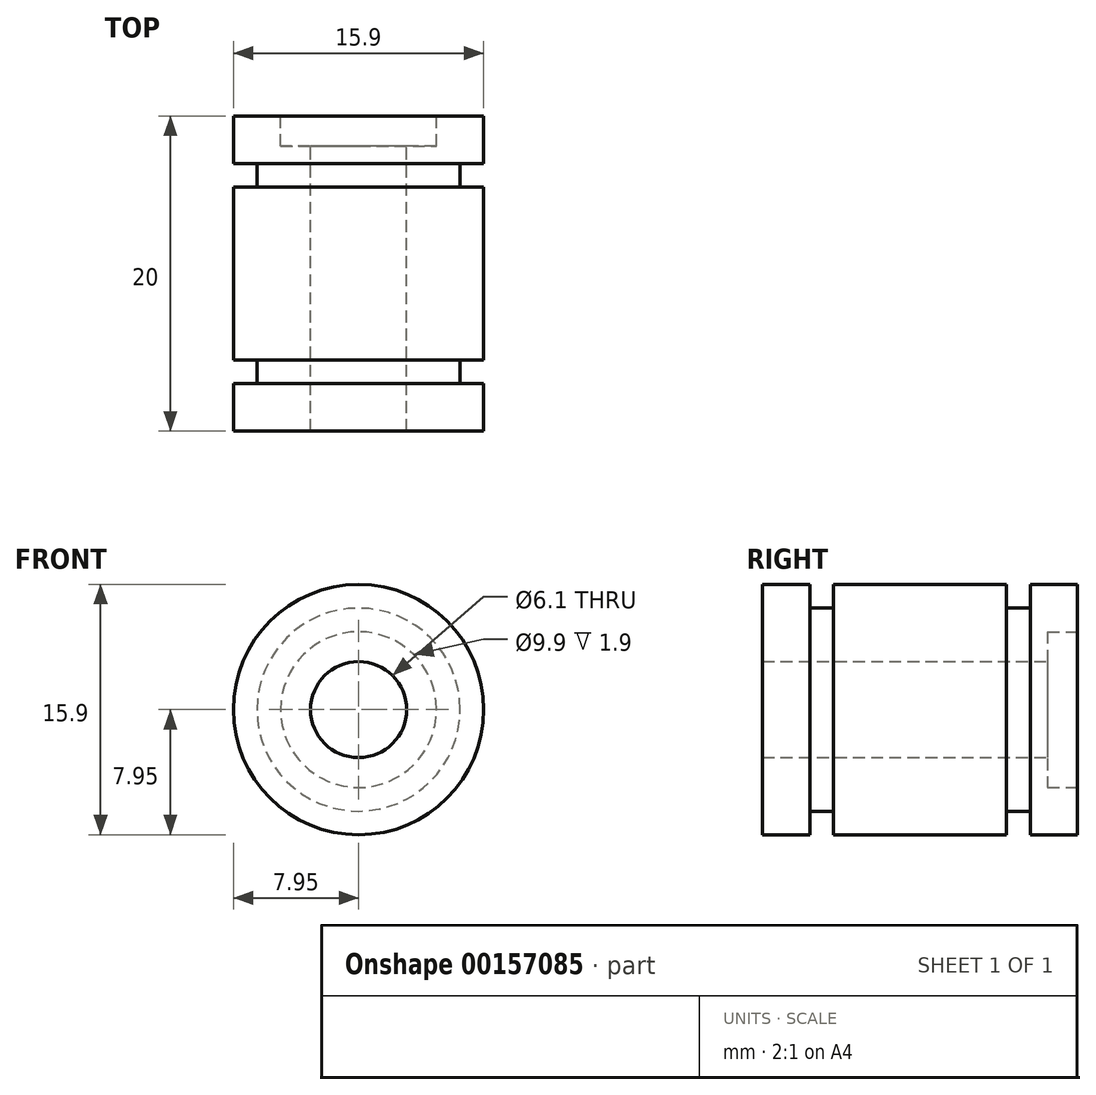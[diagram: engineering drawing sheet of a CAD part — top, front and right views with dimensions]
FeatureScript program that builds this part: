
annotation { "Feature Type Name" : "Feature", "Feature Type Description" : "" }
export const myFeature = defineFeature(function(context is Context, id is Id, definition is map)
    precondition{}
    {
        {
            var Q0;
            Q0=qCreatedBy(makeId("Right.planeOp"),FACE);
            var sketch = newSketch(context, id + "F0", { "sketchPlane" : qUnion([Q0])});
            skLineSegment(sketch, "E0", {"start": v(11.47, 0) * mm, "end": v(0, 0) * mm, "construction": true});
            skLineSegment(sketch, "E1", {"start": v(18.1, 3.05) * mm, "end": v(0, 3.05) * mm});
            skLineSegment(sketch, "E2", {"start": v(18.1, 3.05) * mm, "end": v(18.1, 4.95) * mm});
            skLineSegment(sketch, "E3", {"start": v(20, 4.95) * mm, "end": v(18.1, 4.95) * mm});
            skLineSegment(sketch, "E4", {"start": v(20, 4.95) * mm, "end": v(20, 7.95) * mm});
            skLineSegment(sketch, "E5", {"start": v(17, 7.95) * mm, "end": v(20, 7.95) * mm});
            skLineSegment(sketch, "E6", {"start": v(17, 7.95) * mm, "end": v(17, 6.45) * mm});
            skLineSegment(sketch, "E7", {"start": v(15.5, 6.45) * mm, "end": v(17, 6.45) * mm});
            skLineSegment(sketch, "E8", {"start": v(3, 6.45) * mm, "end": v(3, 7.95) * mm});
            skLineSegment(sketch, "E9", {"start": v(0, 7.95) * mm, "end": v(3, 7.95) * mm});
            skLineSegment(sketch, "E10", {"start": v(0, 7.95) * mm, "end": v(0, 3.05) * mm});
            skLineSegment(sketch, "E11", {"start": v(4.5, 6.45) * mm, "end": v(4.5, 7.95) * mm});
            skLineSegment(sketch, "E12", {"start": v(4.5, 7.95) * mm, "end": v(15.5, 7.95) * mm});
            skLineSegment(sketch, "E13", {"start": v(15.5, 7.95) * mm, "end": v(15.5, 6.45) * mm});
            skLineSegment(sketch, "E14.trimOffspring", {"start": v(4.5, 6.45) * mm, "end": v(3, 6.45) * mm});
            skSolve(sketch);
        }
        {
            var Q0;
            Q0=makeQuery(id+"F0.imprint","IMPRINT",FACE,{"disambiguationData":[TD([[makeQuery(id+"F0.imprint","IMPRINT",EDGE,{"derivedFrom":sQuery(id+"F0.wireOp",EDGE,"E1")}),-1.0]])]});
            var Q1;
            Q1=sQuery(id+"F0.wireOp",EDGE,"E0");
            revolve(context, id + "F1", {"entities" : qUnion([Q0]), "axis" : qUnion([Q1]), "revolveType" : RevolveType.FULL});
        }
    });
